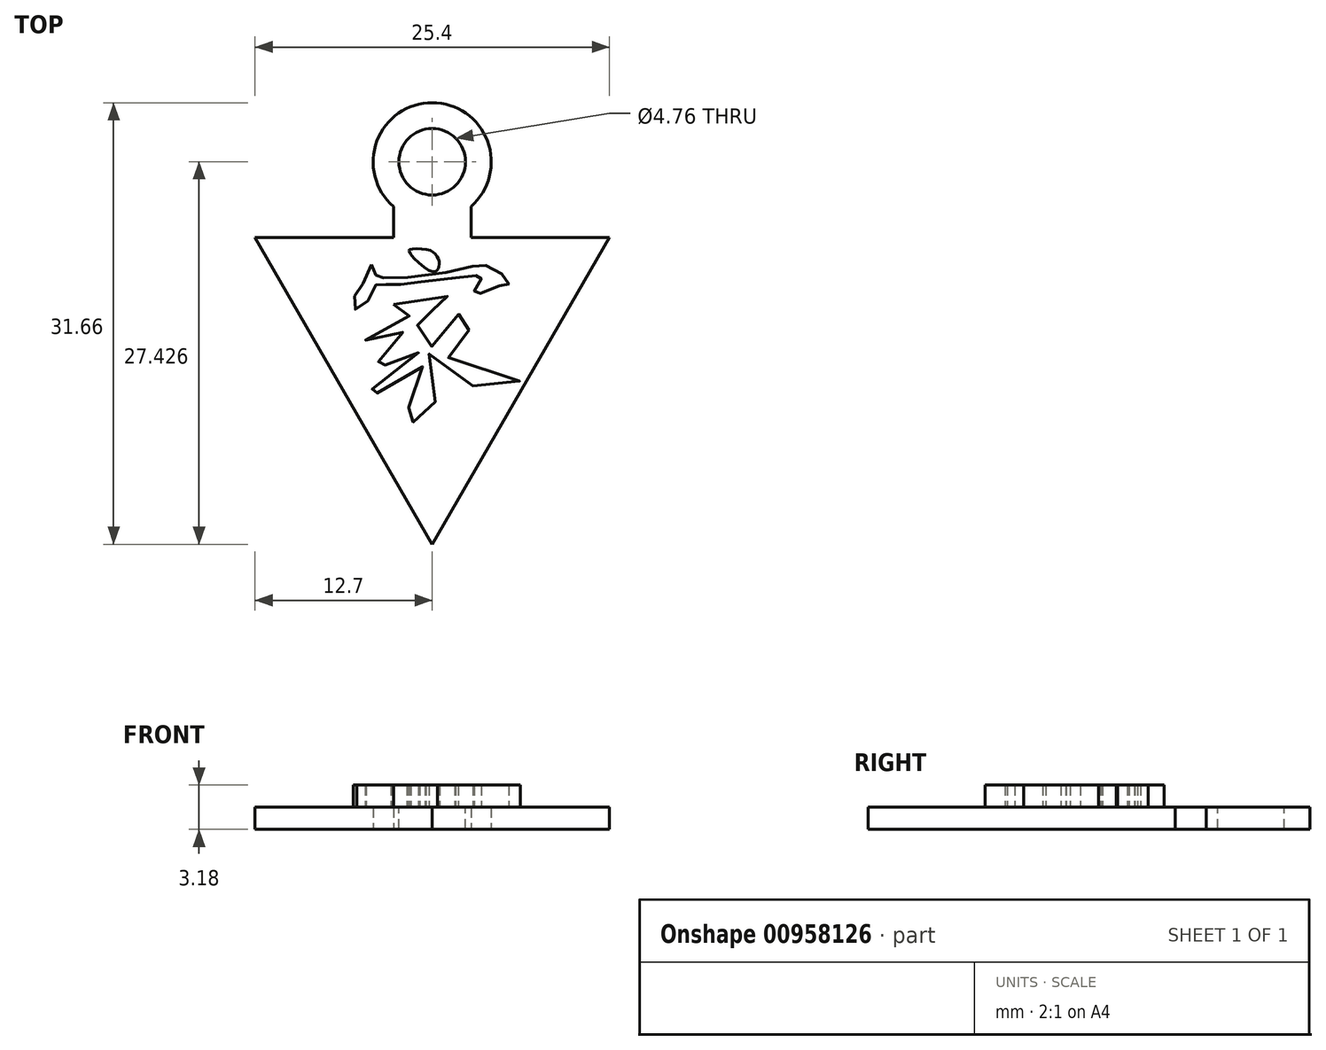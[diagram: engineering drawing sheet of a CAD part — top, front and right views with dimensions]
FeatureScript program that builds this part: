
annotation { "Feature Type Name" : "Feature", "Feature Type Description" : "" }
export const myFeature = defineFeature(function(context is Context, id is Id, definition is map)
    precondition{}
    {
        {
            var Q0;
            Q0=qCreatedBy(makeId("Top.planeOp"),FACE);
            var sketch = newSketch(context, id + "F0", { "sketchPlane" : qUnion([Q0])});
            skCircle(sketch, "E0.cCircle", {"center": v(0, 0) * mm, "radius": 7.33 * mm, "construction": true});
            skLineSegment(sketch, "E0.0", {"start": v(-12.7, 7.33) * mm, "end": v(12.7, 7.33) * mm});
            skLineSegment(sketch, "E0.1", {"start": v(12.7, 7.33) * mm, "end": v(0, -14.66) * mm});
            skLineSegment(sketch, "E0.2", {"start": v(0, -14.66) * mm, "end": v(-12.7, 7.33) * mm});
            skPoint(sketch, "E0.0.midPoint", {"position": v(0, 7.33) * mm});
            skLineSegment(sketch, "E1.bottom", {"start": v(2.77, 14) * mm, "end": v(-2.77, 14) * mm});
            skLineSegment(sketch, "E1.top", {"start": v(2.77, -1.83) * mm, "end": v(-2.77, -1.83) * mm});
            skLineSegment(sketch, "E1.left", {"start": v(2.77, 14) * mm, "end": v(2.77, -1.83) * mm});
            skLineSegment(sketch, "E1.right", {"start": v(-2.77, 14) * mm, "end": v(-2.77, -1.83) * mm});
            skPoint(sketch, "E1.middle", {"position": v(0, 6.08) * mm});
            skCircle(sketch, "E2", {"center": v(0, 12.77) * mm, "radius": 4.23 * mm});
            skSolve(sketch);
        }
        {
            var Q0;
            {var subQ1=sQuery(id+"F0.wireOp",EDGE,"E0.1");Q0=makeQuery(id+"F0.imprint","IMPRINT",FACE,{"disambiguationData":[TD([[makeQuery(id+"F0.imprint","IMPRINT",EDGE,{"derivedFrom":subQ1}),-1.0]])]});}
            var Q1;
            {var subQ5=sQuery(id+"F0.wireOp",EDGE,"E1.top");Q1=makeQuery(id+"F0.imprint","IMPRINT",FACE,{"disambiguationData":[TD([[makeQuery(id+"F0.imprint","IMPRINT",EDGE,{"derivedFrom":subQ5}),-1.0]])]});}
            var Q2;
            {var subQ0=sQuery(id+"F0.wireOp",EDGE,"E1.right");var subQ1=sQuery(id+"F0.wireOp",EDGE,"E0.0");var subQ2=makeQuery(id+"F0.imprint","INTERSECT",VERTEX,{"derivedFrom":[subQ1,subQ0]});Q2=makeQuery(id+"F0.imprint","IMPRINT",FACE,{"disambiguationData":[TD([[makeQuery(id+"F0.imprint","IMPRINT",EDGE,{"disambiguationData":[TD([[subQ2,-1.0]])],"derivedFrom":subQ1}),1.0]])]});}
            var Q3;
            {var subQ0=sQuery(id+"F0.wireOp",EDGE,"E1.bottom");Q3=makeQuery(id+"F0.imprint","IMPRINT",FACE,{"disambiguationData":[TD([[makeQuery(id+"F0.imprint","IMPRINT",EDGE,{"derivedFrom":subQ0}),1.0]])]});}
            var Q4;
            {var subQ0=sQuery(id+"F0.wireOp",EDGE,"E1.bottom");Q4=makeQuery(id+"F0.imprint","IMPRINT",FACE,{"disambiguationData":[TD([[makeQuery(id+"F0.imprint","IMPRINT",EDGE,{"derivedFrom":subQ0}),-1.0]])]});}
            extrude(context, id + "F1", {"entities" : qUnion([Q0, Q1, Q2, Q3, Q4]), "depth" : 1.59 * mm, "offsetDistance" : 25.4 * mm});
        }
        {
            var Q0;
            Q0=makeQuery(id+"F1.opExtrude","CAP_FACE",FACE,{"disambiguationData":[OSD([sQuery(id+"F0.wireOp",EDGE,"E0.0"),sQuery(id+"F0.wireOp",EDGE,"E0.1"),sQuery(id+"F0.wireOp",EDGE,"E0.2"),sQuery(id+"F0.wireOp",EDGE,"E1.left"),sQuery(id+"F0.wireOp",EDGE,"E1.right"),sQuery(id+"F0.wireOp",EDGE,"E2")])],"isStart":false});
            var sketch = newSketch(context, id + "F2", { "sketchPlane" : qUnion([Q0])});
            skFitSpline(sketch, "E3", {"points": [v(-1.67, 6.39) * mm, v(-1.5, 6.5) * mm, v(-0.2, 6.44) * mm, v(0.26, 6.08) * mm, v(0.51, 5.59) * mm, v(0.46, 5.2) * mm, v(0.31, 4.95) * mm, v(-0.2, 4.95) * mm, v(-1.67, 6.39) * mm]});
            skFitSpline(sketch, "E4", {"points": [v(-4.36, 5.4) * mm, v(-4.16, 5.13) * mm, v(-3.93, 4.45) * mm, v(-3.77, 4.43) * mm, v(-2.61, 4.43) * mm, v(2.4, 5.12) * mm, v(3.38, 5.4) * mm, v(4.38, 5.12) * mm, v(5.37, 4.36) * mm, v(5.48, 4) * mm, v(5.12, 3.91) * mm, v(4.65, 3.82) * mm, v(3.01, 3.2) * mm, v(2.9, 3.25) * mm, v(3.44, 4.17) * mm, v(3.52, 4.43) * mm, v(3.47, 4.6) * mm, v(3.25, 4.62) * mm, v(0.52, 4.31) * mm, v(-2.14, 3.98) * mm, v(-2.77, 3.9) * mm, v(-3.93, 4.03) * mm, v(-4.02, 4) * mm, v(-4.15, 3.6) * mm, v(-5.2, 2.17) * mm, v(-5.59, 2.3) * mm, v(-5.57, 3.13) * mm, v(-5.11, 3.72) * mm, v(-4.36, 5.4) * mm]});
            skFitSpline(sketch, "E5", {"points": [v(-2.77, 2.53) * mm, v(-2.32, 2.56) * mm, v(0.72, 3) * mm, v(1.15, 3.12) * mm, v(1.71, 2.89) * mm, v(1.86, 2.6) * mm, v(1.43, 2.38) * mm, v(-0.88, 1.97) * mm, v(-0.88, 1.94) * mm, v(-0.46, 1.58) * mm, v(-0.5, 1.38) * mm, v(-0.74, 1.2) * mm, v(-1.63, 0.72) * mm, v(-1.54, 0.59) * mm, v(-0.55, -0.3) * mm, v(0, -0.46) * mm, v(1.67, 1.19) * mm, v(1.62, 1.78) * mm, v(1.8, 1.85) * mm, v(2.15, 1.72) * mm, v(2.56, 1.5) * mm, v(2.99, 1.02) * mm, v(2.99, 0.83) * mm, v(2.62, 0.68) * mm, v(0.44, -0.6) * mm, v(0.51, -0.65) * mm, v(0.65, -0.8) * mm, v(2.73, -2.16) * mm, v(6.18, -2.93) * mm, v(6.31, -3.06) * mm, v(5.91, -3.27) * mm, v(3.48, -3.48) * mm, v(1.6, -2.25) * mm, v(-0.2, -0.85) * mm, v(-0.2, -1.05) * mm, v(0.11, -1.68) * mm, v(0.37, -3.27) * mm, v(-0.13, -5.4) * mm, v(-0.84, -6.27) * mm, v(-1.13, -6.27) * mm, v(-1.33, -5.93) * mm, v(-2.63, -4.94) * mm, v(-2.77, -4.73) * mm, v(-2.53, -4.7) * mm, v(-1.19, -4.83) * mm, v(-0.57, -3.75) * mm, v(-0.66, -1.95) * mm, v(-0.95, -2.1) * mm, v(-2.1, -3) * mm, v(-4.31, -3.95) * mm, v(-5.23, -4.15) * mm, v(-5.4, -3.97) * mm, v(-4.67, -3.67) * mm, v(-2.94, -2.68) * mm, v(-1, -1.04) * mm, v(-1, -0.87) * mm, v(-1.27, -0.49) * mm, v(-1.39, -0.57) * mm, v(-2.33, -1.32) * mm, v(-4.44, -2.15) * mm, v(-4.69, -2.14) * mm, v(-4.74, -1.96) * mm, v(-4.49, -1.82) * mm, v(-3.2, -1.2) * mm, v(-1.81, 0.12) * mm, v(-1.9, 0.3) * mm, v(-2.08, 0.54) * mm, v(-2.77, 0.26) * mm, v(-4.5, -0.2) * mm, v(-4.72, -0.17) * mm, v(-4.78, 0) * mm, v(-4.36, 0.14) * mm, v(-2.46, 1.08) * mm, v(-1.54, 1.9) * mm, v(-1.79, 2) * mm, v(-2.39, 2) * mm, v(-2.97, 2.4) * mm, v(-2.77, 2.53) * mm]});
            skSolve(sketch);
        }
        {
            var Q0;
            Q0=makeQuery(id+"F2.imprint","IMPRINT",FACE,{"disambiguationData":[TD([[makeQuery(id+"F2.imprint","IMPRINT",EDGE,{"derivedFrom":sQuery(id+"F2.wireOp",EDGE,"E3")}),-1.0]])]});
            var Q1;
            Q1=makeQuery(id+"F2.imprint","IMPRINT",FACE,{"disambiguationData":[TD([[makeQuery(id+"F2.imprint","IMPRINT",EDGE,{"derivedFrom":sQuery(id+"F2.wireOp",EDGE,"E4")}),-1.0]])]});
            var Q2;
            Q2=makeQuery(id+"F2.imprint","IMPRINT",FACE,{"disambiguationData":[TD([[makeQuery(id+"F2.imprint","IMPRINT",EDGE,{"derivedFrom":sQuery(id+"F2.wireOp",EDGE,"E5")}),-1.0]])]});
            extrude(context, id + "F3", {"entities" : qUnion([Q0, Q1, Q2]), "operationType" : NewBodyOperationType.ADD, "depth" : 1.59 * mm, "offsetDistance" : 25.4 * mm});
        }
        {
            var Q0;
            Q0=makeQuery(id+"F1.opExtrude","CAP_FACE",FACE,{"disambiguationData":[OSD([sQuery(id+"F0.wireOp",EDGE,"E0.0"),sQuery(id+"F0.wireOp",EDGE,"E0.1"),sQuery(id+"F0.wireOp",EDGE,"E0.2"),sQuery(id+"F0.wireOp",EDGE,"E1.left"),sQuery(id+"F0.wireOp",EDGE,"E1.right"),sQuery(id+"F0.wireOp",EDGE,"E2")])],"isStart":false});
            var sketch = newSketch(context, id + "F4", { "sketchPlane" : qUnion([Q0])});
            skPoint(sketch, "E6", {"position": v(0, 12.77) * mm});
            skSolve(sketch);
        }
        {
            var Q0;
            Q0=sQuery(id+"F4.wireOp",VERTEX,"E6");
            var Q1;
            Q1=makeQuery(id+"F1.opExtrude","SWEPT_BODY",BODY,{"disambiguationData":[OSD([sQuery(id+"F0.wireOp",EDGE,"E0.0"),sQuery(id+"F0.wireOp",EDGE,"E0.1"),sQuery(id+"F0.wireOp",EDGE,"E0.2"),sQuery(id+"F0.wireOp",EDGE,"E1.left"),sQuery(id+"F0.wireOp",EDGE,"E1.right"),sQuery(id+"F0.wireOp",EDGE,"E2")])]});
            hole(context, id + "F5", {"style" : HoleStyle.SIMPLE, "endStyle" : HoleEndStyle.THROUGH, "holeDiameter" : 4.76 * mm, "majorDiameter" : 6.35 * mm, "isTappedThrough" : true, "tappedDepth" : 12.7 * mm, "tapClearance" : 3, "locations" : qUnion([Q0]), "scope" : qUnion([Q1])});
        }
    });
